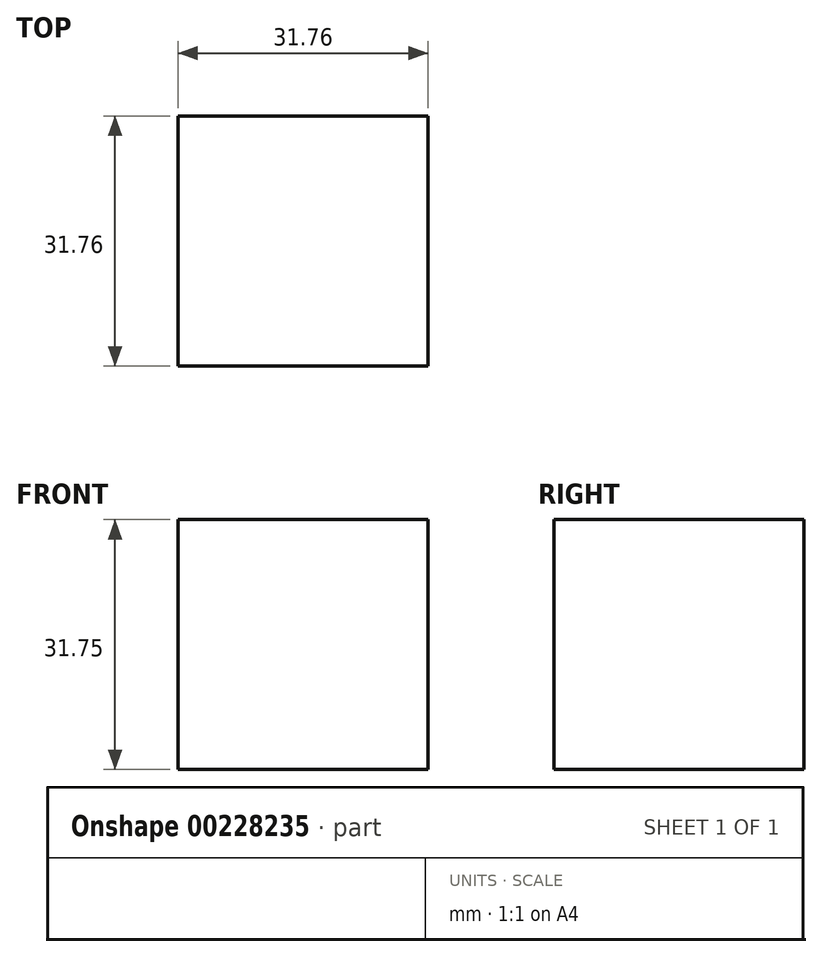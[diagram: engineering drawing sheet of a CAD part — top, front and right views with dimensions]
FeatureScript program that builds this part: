
annotation { "Feature Type Name" : "Feature", "Feature Type Description" : "" }
export const myFeature = defineFeature(function(context is Context, id is Id, definition is map)
    precondition{}
    {
        {
            var Q0;
            Q0=qCreatedBy(makeId("Top.planeOp"),FACE);
            var sketch = newSketch(context, id + "F0", { "sketchPlane" : qUnion([Q0])});
            skLineSegment(sketch, "E0.bottom", {"start": v(-15.88, 15.88) * mm, "end": v(15.88, 15.88) * mm});
            skLineSegment(sketch, "E0.top", {"start": v(-15.88, -15.88) * mm, "end": v(15.88, -15.88) * mm});
            skLineSegment(sketch, "E0.left", {"start": v(-15.87, 15.88) * mm, "end": v(-15.88, -15.88) * mm});
            skLineSegment(sketch, "E0.right", {"start": v(15.88, 15.88) * mm, "end": v(15.88, -15.88) * mm});
            skPoint(sketch, "E0.middle", {"position": v(0, 0) * mm});
            skSolve(sketch);
        }
        {
            var Q0;
            Q0 = qSketchRegion(id + "F0", true);
            extrude(context, id + "F1", {"entities" : qUnion([Q0]), "depth" : 31.75 * mm});
        }
    });
